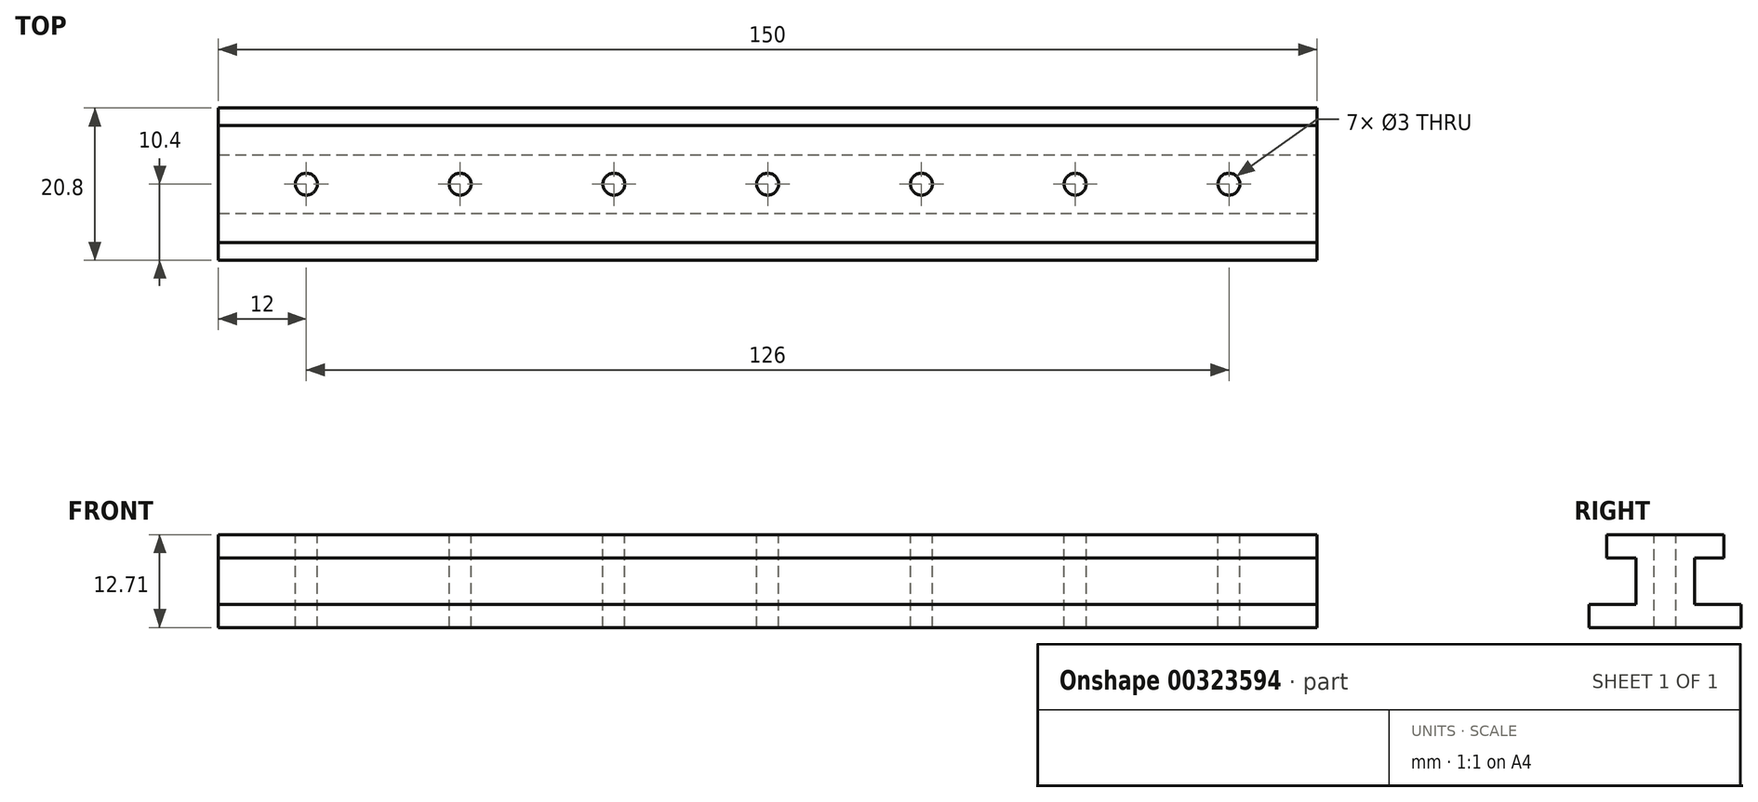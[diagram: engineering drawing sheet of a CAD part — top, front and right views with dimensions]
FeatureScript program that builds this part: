
annotation { "Feature Type Name" : "Feature", "Feature Type Description" : "" }
export const myFeature = defineFeature(function(context is Context, id is Id, definition is map)
    precondition{}
    {
        {
            var Q0;
            Q0=qCreatedBy(makeId("Top.planeOp"),FACE);
            var sketch = newSketch(context, id + "F0", { "sketchPlane" : qUnion([Q0])});
            skLineSegment(sketch, "E0.bottom", {"start": v(0, 0) * mm, "end": v(150, 0) * mm});
            skLineSegment(sketch, "E0.top", {"start": v(0, 8) * mm, "end": v(150, 8) * mm});
            skLineSegment(sketch, "E0.left", {"start": v(0, 0) * mm, "end": v(0, 8) * mm});
            skLineSegment(sketch, "E0.right", {"start": v(150, 0) * mm, "end": v(150, 8) * mm});
            skSolve(sketch);
        }
        {
            var Q0;
            Q0=qSketchRegion(id+"F0",true);
            extrude(context, id + "F1", {"entities" : qUnion([Q0]), "depth" : 6.35 * mm});
        }
        {
            var Q0;
            Q0=makeQuery(id+"F1.opExtrude","CAP_FACE",FACE,{"disambiguationData":[OSD([sQuery(id+"F0.wireOp",EDGE,"E0.bottom"),sQuery(id+"F0.wireOp",EDGE,"E0.top"),sQuery(id+"F0.wireOp",EDGE,"E0.left"),sQuery(id+"F0.wireOp",EDGE,"E0.right")])],"isStart":false});
            var sketch = newSketch(context, id + "F2", { "sketchPlane" : qUnion([Q0])});
            skCircle(sketch, "E1", {"center": v(12, 4) * mm, "radius": 1.5 * mm});
            skCircle(sketch, "E2.1.0.0", {"center": v(33, 4) * mm, "radius": 1.5 * mm});
            skCircle(sketch, "E2.2.0.0", {"center": v(54, 4) * mm, "radius": 1.5 * mm});
            skCircle(sketch, "E2.3.0.0", {"center": v(75, 4) * mm, "radius": 1.5 * mm});
            skCircle(sketch, "E2.4.0.0", {"center": v(96, 4) * mm, "radius": 1.5 * mm});
            skCircle(sketch, "E2.5.0.0", {"center": v(117, 4) * mm, "radius": 1.5 * mm});
            skCircle(sketch, "E2.6.0.0", {"center": v(138, 4) * mm, "radius": 1.5 * mm});
            skLineSegment(sketch, "E2.direction1", {"start": v(12, 4) * mm, "end": v(33, 4) * mm, "construction": true});
            skSolve(sketch);
        }
        {
            var Q0;
            Q0=makeQuery(id+"F1.opExtrude","CAP_FACE",FACE,{"disambiguationData":[OSD([sQuery(id+"F0.wireOp",EDGE,"E0.bottom"),sQuery(id+"F0.wireOp",EDGE,"E0.top"),sQuery(id+"F0.wireOp",EDGE,"E0.left"),sQuery(id+"F0.wireOp",EDGE,"E0.right")])],"isStart":false});
            var sketch = newSketch(context, id + "F3", { "sketchPlane" : qUnion([Q0])});
            skLineSegment(sketch, "E3.bottom", {"start": v(0, 12) * mm, "end": v(150, 12) * mm});
            skLineSegment(sketch, "E3.top", {"start": v(0, -4) * mm, "end": v(150, -4) * mm});
            skLineSegment(sketch, "E3.left", {"start": v(0, 12) * mm, "end": v(0, -4) * mm});
            skLineSegment(sketch, "E3.right", {"start": v(150, 12) * mm, "end": v(150, -4) * mm});
            skSolve(sketch);
        }
        {
            var Q0;
            Q0 = qSketchRegion(id + "F3", true);
            extrude(context, id + "F4", {"entities" : qUnion([Q0]), "operationType" : NewBodyOperationType.ADD, "depth" : 3.17 * mm});
        }
        {
            var Q0;
            Q0=makeQuery(id+"F1.opExtrude","CAP_FACE",FACE,{"disambiguationData":[OSD([sQuery(id+"F0.wireOp",EDGE,"E0.bottom"),sQuery(id+"F0.wireOp",EDGE,"E0.top"),sQuery(id+"F0.wireOp",EDGE,"E0.left"),sQuery(id+"F0.wireOp",EDGE,"E0.right")])],"isStart":true});
            var sketch = newSketch(context, id + "F5", { "sketchPlane" : qUnion([Q0])});
            skLineSegment(sketch, "E4.bottom", {"start": v(0, 6.4) * mm, "end": v(150, 6.4) * mm});
            skLineSegment(sketch, "E4.top", {"start": v(0, -14.4) * mm, "end": v(150, -14.4) * mm});
            skLineSegment(sketch, "E4.left", {"start": v(0, 6.4) * mm, "end": v(0, -14.4) * mm});
            skLineSegment(sketch, "E4.right", {"start": v(150, 6.4) * mm, "end": v(150, -14.4) * mm});
            skSolve(sketch);
        }
        {
            var Q0;
            Q0 = qSketchRegion(id + "F5", true);
            extrude(context, id + "F6", {"entities" : qUnion([Q0]), "operationType" : NewBodyOperationType.ADD, "depth" : 3.17 * mm});
        }
        {
            var Q0;
            Q0=qSketchRegion(id+"F2",true);
            extrude(context, id + "F7", {"entities" : qUnion([Q0]), "operationType" : NewBodyOperationType.REMOVE, "oppositeDirection" : true, "depth" : 25 * mm, "hasSecondDirection" : true, "secondDirectionOppositeDirection" : false, "secondDirectionDepth" : 20.1 * mm});
        }
    });
